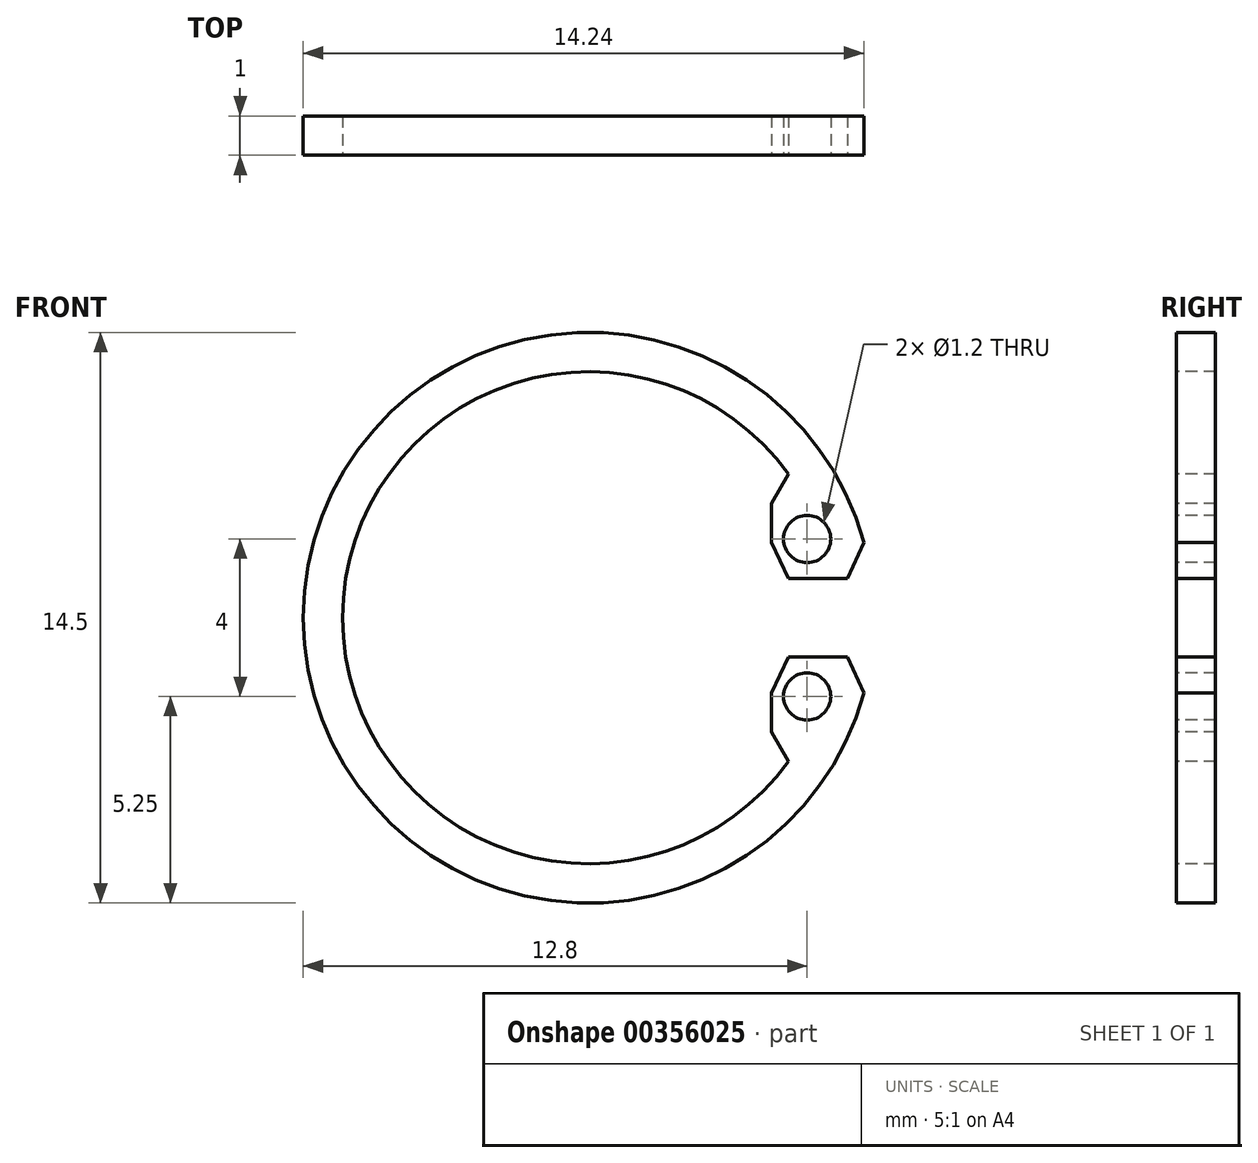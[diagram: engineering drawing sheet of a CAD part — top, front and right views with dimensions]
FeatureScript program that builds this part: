
annotation { "Feature Type Name" : "Feature", "Feature Type Description" : "" }
export const myFeature = defineFeature(function(context is Context, id is Id, definition is map)
    precondition{}
    {
        {
            var Q0;
            Q0=qCreatedBy(makeId("Front.planeOp"),FACE);
            var sketch = newSketch(context, id + "F0", { "sketchPlane" : qUnion([Q0])});
            skArc(sketch, "E0", {"start": v(7, 1.9) * mm, "mid": v(-7.25, 0) * mm, "end": v(7, -1.9) * mm});
            skArc(sketch, "E1", {"start": v(5.08, 3.65) * mm, "mid": v(-6.25, 0) * mm, "end": v(5.08, -3.65) * mm});
            skLineSegment(sketch, "E2", {"start": v(7, 1.9) * mm, "end": v(6.57, 1) * mm});
            skLineSegment(sketch, "E3", {"start": v(6.57, 1) * mm, "end": v(5.07, 1) * mm});
            skLineSegment(sketch, "E4", {"start": v(5.07, 1) * mm, "end": v(4.65, 1.9) * mm});
            skLineSegment(sketch, "E5", {"start": v(4.65, 1.9) * mm, "end": v(4.65, 2.9) * mm});
            skLineSegment(sketch, "E6", {"start": v(4.65, 2.9) * mm, "end": v(5.08, 3.65) * mm});
            skLineSegment(sketch, "E7", {"start": v(-2.64, 0) * mm, "end": v(10.03, 0) * mm, "construction": true});
            skLineSegment(sketch, "E8.MirrorCS", {"start": v(4.65, -2.9) * mm, "end": v(5.08, -3.65) * mm});
            skLineSegment(sketch, "E9.MirrorCS", {"start": v(4.65, -1.9) * mm, "end": v(4.65, -2.9) * mm});
            skLineSegment(sketch, "E10.MirrorCS", {"start": v(5.07, -1) * mm, "end": v(4.65, -1.9) * mm});
            skLineSegment(sketch, "E11.MirrorCS", {"start": v(6.57, -1) * mm, "end": v(5.07, -1) * mm});
            skLineSegment(sketch, "E12.MirrorCS", {"start": v(7, -1.9) * mm, "end": v(6.57, -1) * mm});
            skCircle(sketch, "E13", {"center": v(5.55, 2) * mm, "radius": 0.6 * mm});
            skCircle(sketch, "E14.MirrorC", {"center": v(5.55, -2) * mm, "radius": 0.6 * mm});
            skSolve(sketch);
        }
        {
            var Q0;
            Q0=makeQuery(id+"F0.imprint","IMPRINT",FACE,{"disambiguationData":[TD([[makeQuery(id+"F0.imprint","IMPRINT",EDGE,{"derivedFrom":sQuery(id+"F0.wireOp",EDGE,"E0")}),1.0]])]});
            extrude(context, id + "F1", {"entities" : qUnion([Q0]), "endBound" : BoundingType.SYMMETRIC, "oppositeDirection" : true, "depth" : 1 * mm});
        }
    });
